# Revit family: Żaluzja ścienna ZSR-N
name_source: partatom
category: Urządzenia nawiewne
units: mm (PartAtom-declared; Revit-internal decimal feet)

## family parameters
Numer OmniClass = 23.75.70.21.27.11
Oparty na płaszczyźnie roboczej = Nie
Punkt obliczania pomieszczeń = Nie
Tnij formami wycięć po wczytaniu = Nie
Typ części = Normalny
Tytuł OmniClass = Diffusers, Registers, and Grilles
Współdzielony = Nie
Wymiar okrągłego złącza = Użyj średnicy
Zachowaj orientację opisów = Nie
Zawsze pionowo = Tak

## types (3) — shared parameters
Atest Higieniczny = B-BK-60212-0281/21
Cięgno = Regulacja ręczna - cięgno
Deklaracja zgodności = 11/DZ/2021/K
IfcExportAs = IfcFlowTerminal
Karta katalogowa = https://www.sawpol.pl
Komentarze typu = Żaluzja ścienna
Maksymalna szerokość otworu montażowego = 2400 mm
Maksymalna wysokość otworu montażowego = 2400 mm
Minimalna szerokość otworu montażowego = 300 mm
Minimalna wysokość otworu montażowego = 650 mm  [stored 2.13255 ft]
Model = ZSR-N
Montaż niewidoczny wąsy = Montaż niewidoczny za pomocą wkrętów oraz wąsów
Montaż niewidoczny za pomocą kątowników w ramie montażowej = Montaż niewidoczny za pomocą kątowników w ramie montażowej
Montaż niewidoczny za pomocą kątowników w ramie montażowej dedykowany do montażu czerpni w płycie warstwowej = Montaż niewidoczny za pomocą kątowników w ramie montażowej dedykowany do montażu czerpni w płycie warstwowej
Montaż widoczny na wkręty = Montaż widoczny na wkręty
Obraz typu = ZSR.png
Producent = PPHU SAW-POL
Siłownik 1 = Siłownik Belimo
Siłownik 2 = Inny siłownik
Sterowanie ręczne = Regulacja ręczna
URL = https://www.sawpol.pl
zero-valued in all types: Domyślna rzędna

## per-type parameters (varying)
| type | Materiał | Materiał piór | Wykonanie aluminium | Wykonanie stal nierdzewna | Wykonanie stal ocynkowana |
| OC | SAW_POL Stal ocynkowana | SAW_POL Stal ocynkowana | Nie | Nie | Tak |
| AL | SAW_POL Aluminium | SAW_POL Aluminium | Tak | Nie | Nie |
| KO | SAW-POL Stal nierdzewna | SAW-POL Stal nierdzewna | Nie | Tak | Nie |

note: [stored X ft] marks values corroborated as IEEE doubles in the binary element streams (Revit-internal decimal feet)
